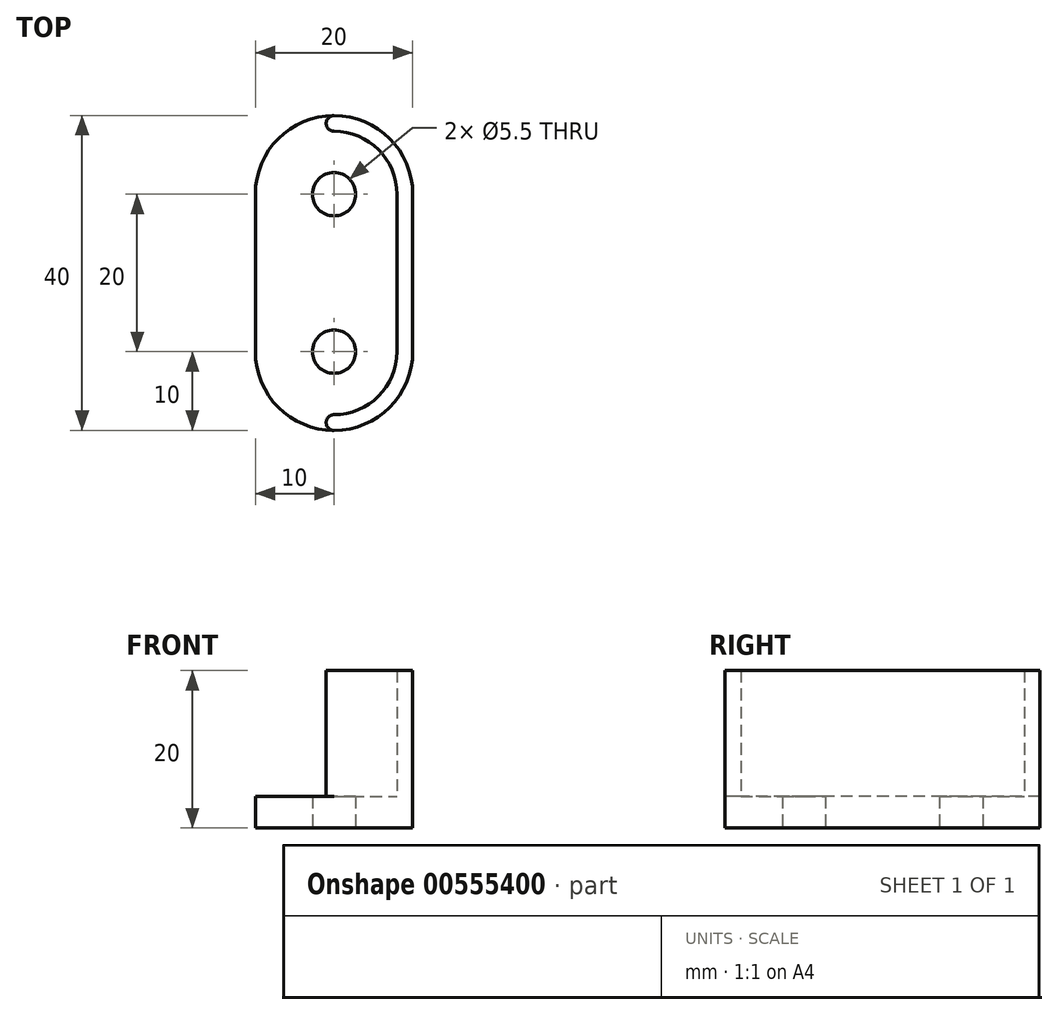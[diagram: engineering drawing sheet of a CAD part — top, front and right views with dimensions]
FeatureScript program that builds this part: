
annotation { "Feature Type Name" : "Feature", "Feature Type Description" : "" }
export const myFeature = defineFeature(function(context is Context, id is Id, definition is map)
    precondition{}
    {
        {
            var Q0;
            Q0=qCreatedBy(makeId("Top.planeOp"),FACE);
            var sketch = newSketch(context, id + "F0", { "sketchPlane" : qUnion([Q0])});
            skCircle(sketch, "E0", {"center": v(0, 0) * mm, "radius": 2.75 * mm});
            skCircle(sketch, "E1", {"center": v(0, 20) * mm, "radius": 2.75 * mm});
            skLineSegment(sketch, "E2", {"start": v(-10, 20) * mm, "end": v(-10, 0) * mm});
            skLineSegment(sketch, "E3", {"start": v(-10, 10) * mm, "end": v(10, 10) * mm, "construction": true});
            skLineSegment(sketch, "E4", {"start": v(0, -10) * mm, "end": v(0, 30) * mm, "construction": true});
            skLineSegment(sketch, "E5", {"start": v(10, 0) * mm, "end": v(10, 20) * mm});
            skCircle(sketch, "E6", {"center": v(0, 0) * mm, "radius": 5 * mm, "construction": true});
            skCircle(sketch, "E7", {"center": v(0, 20) * mm, "radius": 5 * mm, "construction": true});
            skLineSegment(sketch, "E8.0", {"start": v(0, -8) * mm, "end": v(0, -8) * mm});
            skLineSegment(sketch, "E8.3", {"start": v(8, 0) * mm, "end": v(8, 20) * mm});
            skArc(sketch, "E8.4", {"start": v(0, -8) * mm, "mid": v(5.66, -5.66) * mm, "end": v(8, 0) * mm});
            skLineSegment(sketch, "E9.MirrorCS", {"start": v(-10, 0) * mm, "end": v(-10, 20) * mm});
            skLineSegment(sketch, "E10.MirrorCS", {"start": v(10, 20) * mm, "end": v(10, 0) * mm});
            skArc(sketch, "E11", {"start": v(10, 20) * mm, "mid": v(0, 30) * mm, "end": v(-10, 20) * mm});
            skArc(sketch, "E12", {"start": v(-10, 0) * mm, "mid": v(0, -10) * mm, "end": v(10, 0) * mm});
            skArc(sketch, "E13", {"start": v(0, -8) * mm, "mid": v(-1, -9) * mm, "end": v(0, -10) * mm});
            skArc(sketch, "E14.MirrorCS", {"start": v(0, 28) * mm, "mid": v(-1, 29) * mm, "end": v(0, 30) * mm});
            skArc(sketch, "E15.MirrorCS", {"start": v(0, 28) * mm, "mid": v(5.66, 25.66) * mm, "end": v(8, 20) * mm});
            skSolve(sketch);
        }
        {
            var Q0;
            Q0=makeQuery(id+"F0.imprint","IMPRINT",FACE,{"disambiguationData":[TD([[makeQuery(id+"F0.imprint","IMPRINT",EDGE,{"derivedFrom":sQuery(id+"F0.wireOp",EDGE,"E0")}),-1.0]])]});
            extrude(context, id + "F1", {"entities" : qUnion([Q0]), "depth" : 4 * mm, "offsetDistance" : 25 * mm});
        }
        {
            var Q0;
            Q0=makeQuery(id+"F0.imprint","IMPRINT",FACE,{"disambiguationData":[TD([[makeQuery(id+"F0.imprint","IMPRINT",EDGE,{"derivedFrom":sQuery(id+"F0.wireOp",EDGE,"E8.3")}),-1.0]])]});
            extrude(context, id + "F2", {"entities" : qUnion([Q0]), "operationType" : NewBodyOperationType.ADD, "depth" : 20 * mm, "offsetDistance" : 25 * mm});
        }
    });
